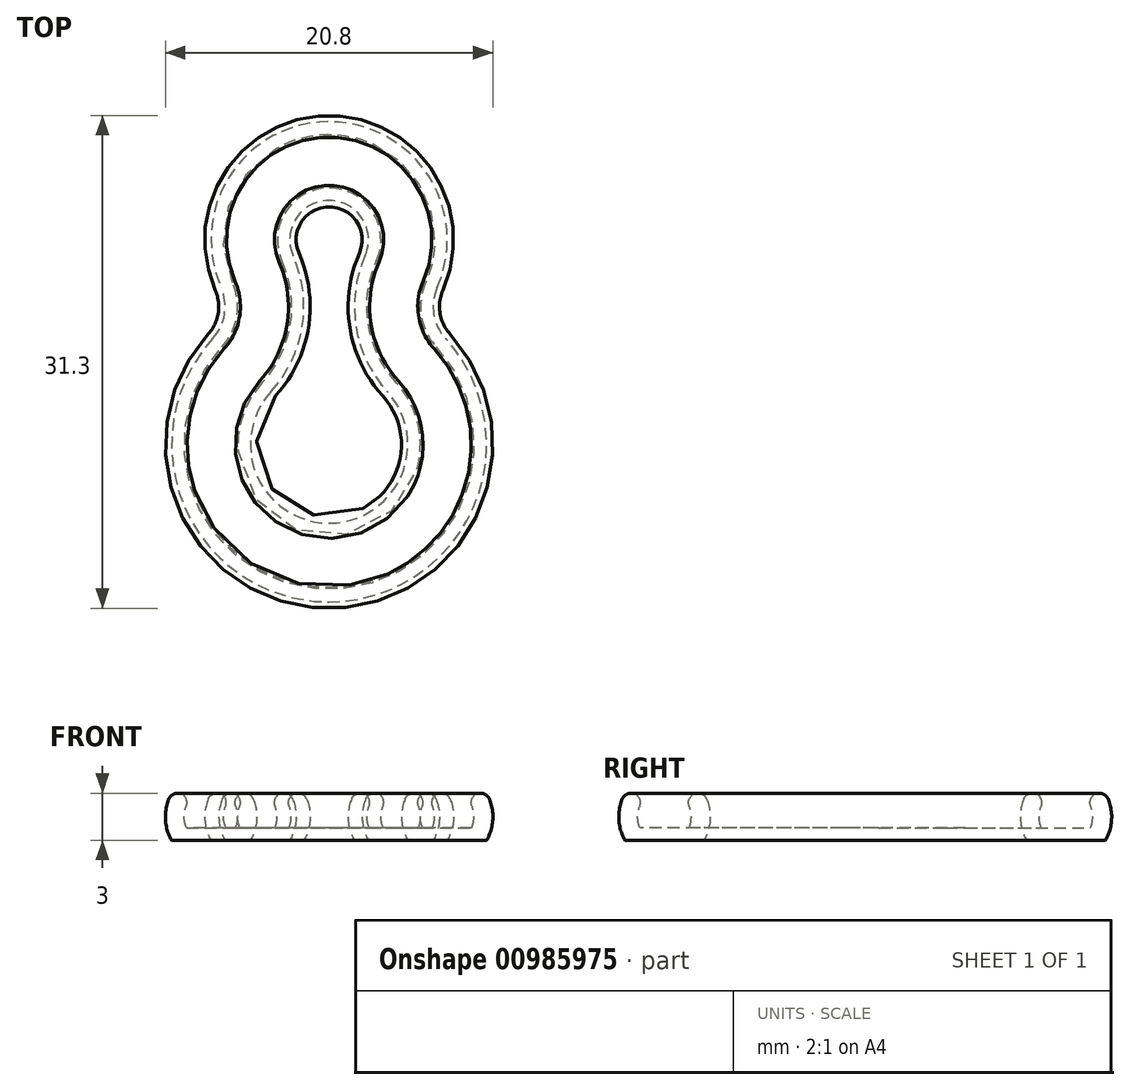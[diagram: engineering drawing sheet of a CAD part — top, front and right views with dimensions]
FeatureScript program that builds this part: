
annotation { "Feature Type Name" : "Feature", "Feature Type Description" : "" }
export const myFeature = defineFeature(function(context is Context, id is Id, definition is map)
    precondition{}
    {
        {
            var Q0;
            Q0=qCreatedBy(makeId("Top.planeOp"),FACE);
            var sketch = newSketch(context, id + "F0", { "sketchPlane" : qUnion([Q0])});
            skArc(sketch, "E0", {"start": v(-7.39, 6.74) * mm, "mid": v(0, -10) * mm, "end": v(7.39, 6.74) * mm});
            skArc(sketch, "E1", {"start": v(6.86, 9.97) * mm, "mid": v(0, 20.5) * mm, "end": v(-6.86, 9.97) * mm});
            skPoint(sketch, "E2.visualSharp", {"position": v(5.75, 8.18) * mm});
            skArc(sketch, "E2.filletArc", {"start": v(6.86, 9.97) * mm, "mid": v(6.64, 8.28) * mm, "end": v(7.39, 6.74) * mm});
            skPoint(sketch, "E3.visualSharp", {"position": v(-5.75, 8.18) * mm});
            skArc(sketch, "E3.filletArc", {"start": v(-7.39, 6.74) * mm, "mid": v(-6.64, 8.28) * mm, "end": v(-6.86, 9.97) * mm});
            skArc(sketch, "E4.0", {"start": v(2.29, 12) * mm, "mid": v(0, 15.5) * mm, "end": v(-2.29, 12) * mm});
            skArc(sketch, "E4.1", {"start": v(2.29, 12) * mm, "mid": v(1.71, 7.47) * mm, "end": v(3.7, 3.37) * mm});
            skArc(sketch, "E4.2", {"start": v(-3.7, 3.37) * mm, "mid": v(0, -5) * mm, "end": v(3.7, 3.37) * mm});
            skArc(sketch, "E4.3", {"start": v(-3.7, 3.37) * mm, "mid": v(-1.71, 7.47) * mm, "end": v(-2.29, 12) * mm});
            skLineSegment(sketch, "E5", {"start": v(-10, 0) * mm, "end": v(10, 0) * mm, "construction": true});
            skPoint(sketch, "E6", {"position": v(5, 0) * mm});
            skSolve(sketch);
        }
        {
            var Q0;
            Q0=qCreatedBy(makeId("Front.planeOp"),FACE);
            var sketch = newSketch(context, id + "F1", { "sketchPlane" : qUnion([Q0])});
            skArc(sketch, "E7", {"start": v(8.4, 0) * mm, "mid": v(9.2, 1.5) * mm, "end": v(8.4, 3) * mm});
            skArc(sketch, "E8.0", {"start": v(10, 0) * mm, "mid": v(10.4, 1.5) * mm, "end": v(10, 3) * mm});
            skLineSegment(sketch, "E9", {"start": v(8.4, 0) * mm, "end": v(10, 0) * mm});
            skLineSegment(sketch, "E10", {"start": v(8.4, 3) * mm, "end": v(10, 3) * mm});
            skArc(sketch, "E11", {"start": v(6.6, 3) * mm, "mid": v(5.8, 1.5) * mm, "end": v(6.6, 0) * mm});
            skArc(sketch, "E12.0", {"start": v(5, 3) * mm, "mid": v(4.6, 1.5) * mm, "end": v(5, 0) * mm});
            skLineSegment(sketch, "E13", {"start": v(6.6, 0) * mm, "end": v(5, 0) * mm});
            skLineSegment(sketch, "E14", {"start": v(5, 3) * mm, "end": v(6.6, 3) * mm});
            skSolve(sketch);
        }
        {
            var Q0;
            Q0=makeQuery(id+"F1.imprint","IMPRINT",FACE,{"disambiguationData":[TD([[makeQuery(id+"F1.imprint","IMPRINT",EDGE,{"derivedFrom":sQuery(id+"F1.wireOp",EDGE,"E7")}),-1.0]])]});
            var Q1;
            Q1=sQuery(id+"F0.wireOp",EDGE,"E0");
            var Q2;
            Q2=sQuery(id+"F0.wireOp",EDGE,"E2.filletArc");
            var Q3;
            Q3=sQuery(id+"F0.wireOp",EDGE,"E1");
            var Q4;
            Q4=sQuery(id+"F0.wireOp",EDGE,"E3.filletArc");
            sweep(context, id + "F2", {"profiles" : qUnion([Q0]), "path" : qUnion([Q1, Q2, Q3, Q4])});
        }
        {
            var Q0;
            Q0=makeQuery(id+"F0.imprint","IMPRINT",FACE,{"disambiguationData":[TD([[makeQuery(id+"F0.imprint","IMPRINT",EDGE,{"derivedFrom":sQuery(id+"F0.wireOp",EDGE,"E0")}),1.0]])]});
            extrude(context, id + "F3", {"entities" : qUnion([Q0]), "operationType" : NewBodyOperationType.ADD, "depth" : .8 * mm, "offsetDistance" : 25 * mm});
        }
        {
            var Q0;
            Q0=makeQuery(id+"F1.imprint","IMPRINT",FACE,{"disambiguationData":[TD([[makeQuery(id+"F1.imprint","IMPRINT",EDGE,{"derivedFrom":sQuery(id+"F1.wireOp",EDGE,"E11")}),-1.0]])]});
            var Q1;
            Q1=sQuery(id+"F0.wireOp",EDGE,"E4.2");
            var Q2;
            Q2=sQuery(id+"F0.wireOp",EDGE,"E4.1");
            var Q3;
            Q3=sQuery(id+"F0.wireOp",EDGE,"E4.0");
            var Q4;
            Q4=sQuery(id+"F0.wireOp",EDGE,"E4.3");
            sweep(context, id + "F4", {"operationType" : NewBodyOperationType.ADD, "profiles" : qUnion([Q0]), "path" : qUnion([Q1, Q2, Q3, Q4])});
        }
        {
            var Q0;
            Q0=makeQuery(id+"F2.opSweep","SWEPT_EDGE",EDGE,{"disambiguationData":[OSD([sQuery(id+"F0.wireOp",EDGE,"E0"),sQuery(id+"F1.wireOp",EDGE,"E7"),sQuery(id+"F1.wireOp",EDGE,"E10")])]});
            var Q1;
            Q1=makeQuery(id+"F2.opSweep","SWEPT_EDGE",EDGE,{"disambiguationData":[OSD([sQuery(id+"F0.wireOp",EDGE,"E2.filletArc"),sQuery(id+"F1.wireOp",EDGE,"E8.0"),sQuery(id+"F1.wireOp",EDGE,"E10")])]});
            var Q2;
            Q2=makeQuery(id+"F4.opSweep","SWEPT_EDGE",EDGE,{"disambiguationData":[OSD([sQuery(id+"F0.wireOp",EDGE,"E4.1"),sQuery(id+"F1.wireOp",EDGE,"E12.0"),sQuery(id+"F1.wireOp",EDGE,"E14")])]});
            var Q3;
            Q3=makeQuery(id+"F4.opSweep","SWEPT_EDGE",EDGE,{"disambiguationData":[OSD([sQuery(id+"F0.wireOp",EDGE,"E4.1"),sQuery(id+"F1.wireOp",EDGE,"E11"),sQuery(id+"F1.wireOp",EDGE,"E14")])]});
            fillet(context, id + "F5", {"entities" : qUnion([Q0, Q1, Q2, Q3]), "radius" : .6 * mm, "tangentPropagation" : true, "allowEdgeOverflow" : false});
        }
    });
